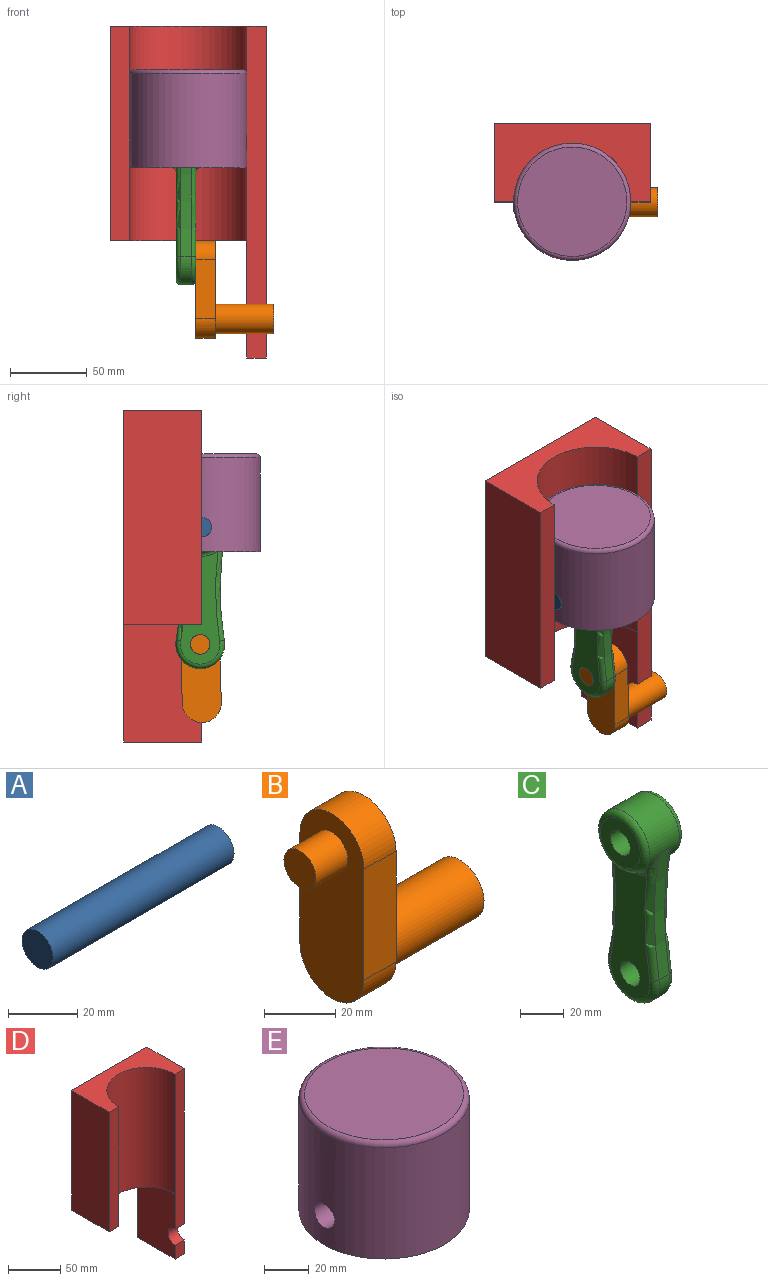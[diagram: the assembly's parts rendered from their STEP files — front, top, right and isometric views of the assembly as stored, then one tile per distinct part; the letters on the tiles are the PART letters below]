
ASSEMBLY  parts=5 mates=5
PART A: 3 faces, bbox 73.7x12.7x12.7 mm
  f0: cylinder r=6.35mm len=73.66mm, axis (1,0,0), area 2938.9mm2, adj f1,f2
  f1: plane 12.7x12.7mm, normal (-1,0,0), area 126.7mm2, adj f0
  f2: plane 12.7x12.7mm, normal (1,0,0), area 126.7mm2, adj f0
PART B: 10 faces, bbox 63.5x25.4x63.5 mm
  f0: cylinder r=9.53mm len=38.1mm, axis (-1,0,0), area 2280.2mm2, adj f1,f2
  f1: plane 19.05x19.05mm, normal (1,0,0), area 285mm2, adj f0
  f2: plane 63.5x25.4mm, normal (1,0,0), area 1189.4mm2, adj f0,f3,f4,f5,f6
  f3: plane 38.1x12.7mm, normal (0,-1,0), area 483.9mm2, adj f2,f4,f6,f7
  f4: cylinder r=12.7mm len=25.4mm, axis (-1,0,0), area 506.7mm2, adj f2,f3,f5,f7
  f5: plane 38.1x12.7mm, normal (0,1,0), area 483.9mm2, adj f2,f4,f6,f7
  f6: cylinder r=12.7mm len=25.4mm, axis (-1,0,0), area 506.7mm2, adj f2,f3,f5,f7
  f7: plane 63.5x25.4mm, normal (-1,0,0), area 1347.8mm2, adj f3,f4,f5,f6,f8
  f8: cylinder r=6.35mm len=12.7mm, axis (-1,0,0), area 506.7mm2, adj f7,f9
  f9: plane 12.7x12.7mm, normal (-1,0,0), area 126.7mm2, adj f8
PART C: 24 faces, bbox 25.4x34.4x110.6 mm
  f0: cylinder r=15.88mm len=31.75mm, axis (-1,0,0), area 1209.7mm2, adj f4,f6,f10,f11,f13,f16,f17,f18
  f1: cylinder r=6.35mm len=25.4mm, axis (-1,0,0), area 1013.4mm2, adj f2,f3
  f2: plane 25.65x25.65mm, normal (1,0,0), area 390.2mm2, adj f1,f23
  f3: plane 25.65x25.65mm, normal (-1,0,0), area 390.2mm2, adj f1,f22
  f4: cylinder r=203.2mm len=70.68mm, axis (-1,0,0), area 469.1mm2, adj f0,f5,f12,f19
  f5: cylinder r=15.88mm len=31.75mm, axis (-1,0,0), area 366mm2, adj f4,f6,f14,f21
  f6: cylinder r=203.2mm len=70.68mm, axis (-1,0,0), area 469.1mm2, adj f0,f5,f15,f20
  f7: cylinder r=6.35mm len=12.7mm, axis (-1,0,0), area 506.7mm2, adj f8,f9
  f8: plane 73.43x25.65mm, normal (1,0,0), area 1341.4mm2, adj f7,f16,f19,f20,f21
  f9: plane 73.43x25.65mm, normal (-1,0,0), area 1341.4mm2, adj f7,f11,f12,f14,f15
  f10: bspline ~14x8.12mm, area 32.3mm2, adj f0,f11,f12
  f11: torus R=18.92mm, axis (1,0,0), area 97.9mm2, adj f0,f9,f10,f13
  f12: torus R=206.25mm, axis (1,0,0), area 306.4mm2, adj f4,f9,f10,f14
  f13: bspline ~14x8.12mm, area 32.3mm2, adj f0,f11,f15
  f14: torus R=12.83mm, axis (1,0,0), area 246.8mm2, adj f5,f9,f12,f15
  f15: torus R=206.25mm, axis (1,0,0), area 306.4mm2, adj f6,f9,f13,f14
  f16: torus R=18.92mm, axis (1,0,0), area 97.9mm2, adj f0,f8,f17,f18
  f17: bspline ~14x8.12mm, area 32.3mm2, adj f0,f16,f19
  f18: bspline ~14x8.12mm, area 32.3mm2, adj f0,f16,f20
  f19: torus R=206.25mm, axis (1,0,0), area 306.4mm2, adj f4,f8,f17,f21
  f20: torus R=206.25mm, axis (1,0,0), area 306.4mm2, adj f6,f8,f18,f21
  f21: torus R=12.83mm, axis (1,0,0), area 246.8mm2, adj f5,f8,f19,f20
  f22: torus R=12.83mm, axis (1,0,0), area 444.2mm2, adj f0,f3
  f23: torus R=12.83mm, axis (1,0,0), area 444.2mm2, adj f0,f2
PART D: 12 faces, bbox 101.6x50.8x215.9 mm
  f0: plane 180.98x12.7mm, normal (0,-1,0), area 2298.4mm2, adj f1,f3,f5,f9,f11
  f1: plane 76.2x50.8mm, normal (-1,0,0), area 3728.4mm2, adj f0,f2,f4,f6,f10,f11
  f2: plane 88.9x50.8mm, normal (0,0,-1), area 2235.9mm2, adj f1,f3,f6,f7,f8
  f3: cylinder r=38.1mm len=139.7mm, axis (0,0,-1), area 16721.3mm2, adj f0,f2,f8,f9
  f4: plane 15.88x12.7mm, normal (0,-1,0), area 201.6mm2, adj f1,f5,f10,f11
  f5: plane 215.9x50.8mm, normal (1,0,0), area 10825.2mm2, adj f0,f4,f6,f9,f10,f11
  f6: plane 215.9x101.6mm, normal (0,1,0), area 15161.3mm2, adj f1,f2,f5,f7,f9,f10
  f7: plane 139.7x50.8mm, normal (-1,0,0), area 7096.8mm2, adj f2,f6,f8,f9
  f8: plane 139.7x12.7mm, normal (0,-1,0), area 1774.2mm2, adj f2,f3,f7,f9
  f9: plane 101.6x50.8mm, normal (0,0,1), area 2881.1mm2, adj f0,f3,f5,f6,f7,f8
  f10: plane 50.8x12.7mm, normal (0,0,-1), area 645.2mm2, adj f1,f4,f5,f6
  f11: cylinder r=9.53mm len=19.05mm, axis (1,0,0), area 380mm2, adj f0,f1,f4,f5
PART E: 11 faces, bbox 82.5x82.5x63.5 mm
  f0: plane 57.15x38.1mm, normal (-1,0,0), area 2050.7mm2, adj f2,f3,f6,f7,f9
  f1: plane 57.15x38.1mm, normal (1,0,0), area 2050.7mm2, adj f2,f3,f6,f8,f9
  f2: cylinder r=31.27mm len=38.1mm, axis (0,0,-1), area 996.5mm2, adj f0,f1,f6,f9
  f3: cylinder r=31.27mm len=38.1mm, axis (0,0,-1), area 996.5mm2, adj f0,f1,f6,f9
  f4: plane 71.12x71.12mm, normal (0,0,1), area 3972.6mm2, adj f10
  f5: cylinder r=38.1mm len=76.2mm, axis (0,0,-1), area 14339.1mm2, adj f6,f7,f8,f10
  f6: plane 76.2x76.2mm, normal (0,0,-1), area 3016.7mm2, adj f0,f1,f2,f3,f5
  f7: cylinder r=6.35mm len=25.4mm, axis (1,0,0), area 1002.8mm2, adj f0,f5
  f8: cylinder r=6.35mm len=25.4mm, axis (1,0,0), area 1002.8mm2, adj f1,f5
  f9: plane 62.54x25.4mm, normal (0,0,-1), area 1543.7mm2, adj f0,f1,f2,f3
  f10: torus R=35.56mm, axis (0,0,1), area 932mm2, adj f4,f5
PLACE A rot(axis=(-1,0,0),11deg) t=(-52.23,32.21,-36.62)mm
PLACE B rot(axis=(-1,0,0),1.6deg) t=(-52.23,52.17,-1.41)mm
PLACE C rot(axis=(1,0,0),0.8deg) t=(-52.23,52.05,-27.89)mm
PLACE D t=(-50.8,50.8,0)mm fixed
PLACE E t=(-50.8,50.8,-28.6)mm
MATE revolute A.f0 <-> C.f0  axis (1,0,0) through (-1.43,0,63.48)mm
MATE cylindrical E.f7 <-> A.f0  axis (1,0,0) through (-38.26,0,63.48)mm
MATE slider D.f3 <-> E.f2  axis (0,0,1) through (0,0,139.7)mm
MATE cylindrical B.f0 <-> D.f11  axis (-1,0,0) through (36.67,0,-50.8)mm
MATE revolute C.f5 <-> B.f6  axis (-1,0,0) through (-7.78,1.04,-12.71)mm
